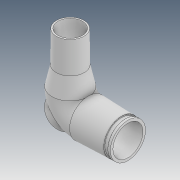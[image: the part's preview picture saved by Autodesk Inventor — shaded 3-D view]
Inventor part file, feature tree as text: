
AUTODESK INVENTOR PART (.ipt)
format: ipt  version: 2020 (Build 240168000, 168)  size: 233,984 bytes
history: native  units: mm
features: sketch x7, revolve x4, plane x3, extrude x2
ambient origin geometry x8: Origin, YZ Plane, XZ Plane, XY Plane, X Axis, Y Axis, Z Axis, Center Point
bodies: Solid1 (feature_tree)
feature tree (16):
  revolve  "Revolution1"  [1 undecoded]
  plane  "Work Plane1"
  sketch  "Sketch2"  dims[d2=14.0mm d3=1.6mm]
  revolve  "Revolution2"  [1 undecoded]
  revolve  "Revolution3"  [1 undecoded]
  plane  "Work Plane3"
  extrude  "Extrusion1"  TaperAngle=90.0deg  [1 undecoded]
  extrude  "Extrusion2"  TaperAngle=90.0deg  [1 undecoded]
  revolve  "Revolution4"  [1 undecoded]
  sketch  "Sketch1"  dims[d0=14.5mm d1=31.6mm]
  sketch  "Sketch3"  dims[d4=13.2mm d5=2.0mm]
  sketch  "Sketch4"  dims[d6=3.2mm d7=90.0deg]
  plane  "Work Plane2"
  sketch  "Sketch5"  dims[d8=14.5mm d9=90.0deg]
  sketch  "Sketch6"  dims[d10=15.0mm d11=11.25mm]
  sketch  "Sketch7"  dims[d12=25.0mm d13=11.0mm d14=1.2mm d15=1.2mm d17=90.0deg d18=135.0deg d19=28.0mm d20=10.0mm d21=0.0mm d22=2.0mm d23=25.0mm d24=0.6mm d25=0.0mm d26=15.0mm d27=90.0deg]
note: 6 required parameter values undecoded (feature->parameter linkage not recoverable at this tier; creation-order binding heuristic only, values carry confidence <= 0.55)